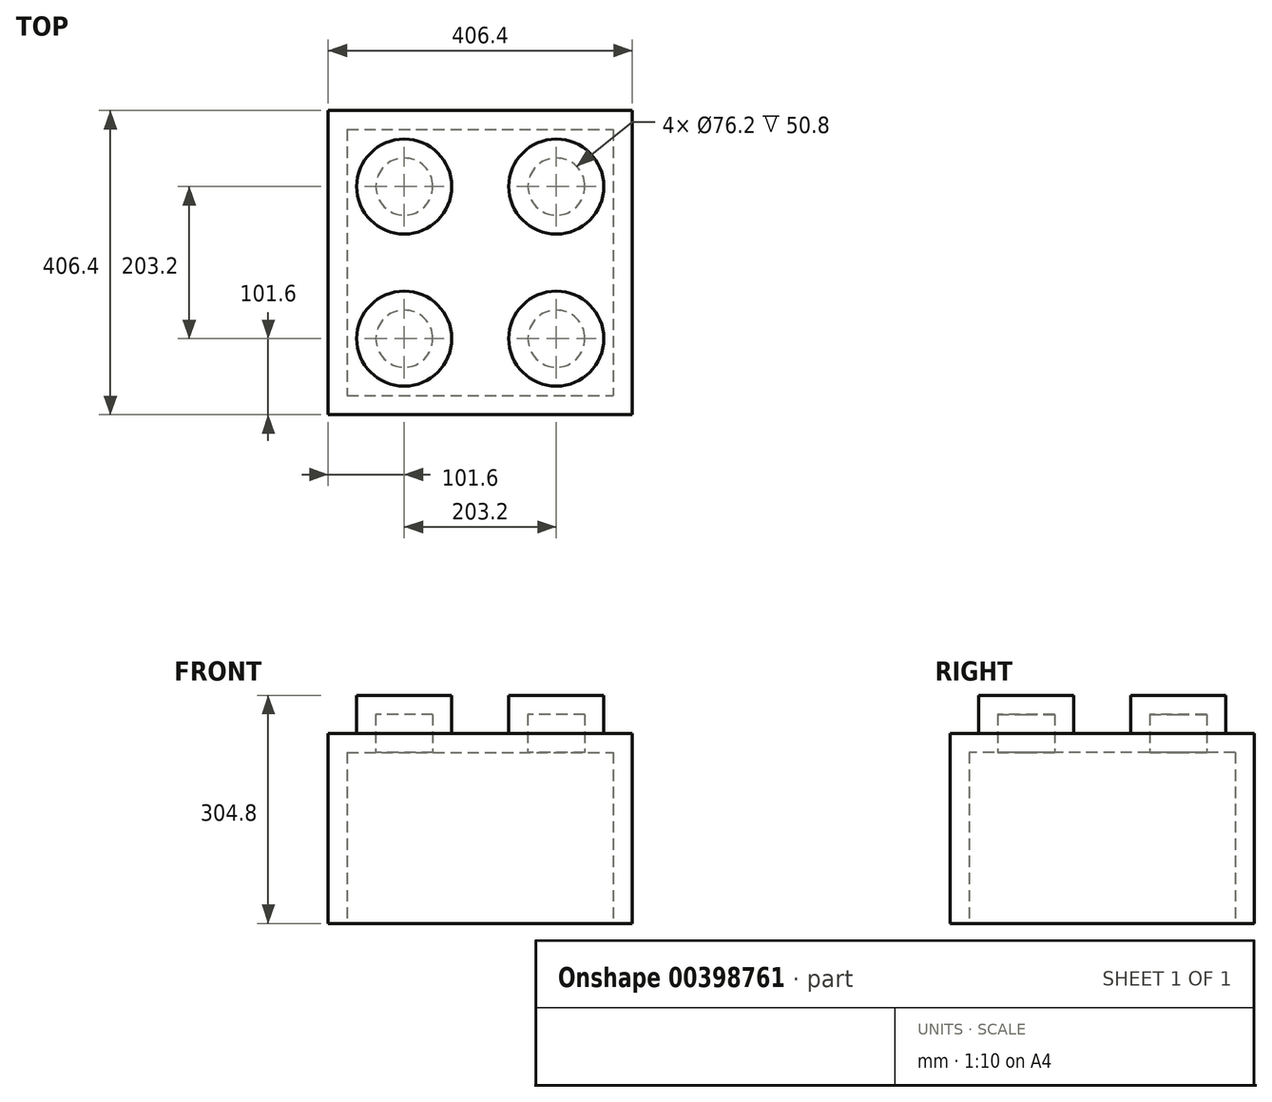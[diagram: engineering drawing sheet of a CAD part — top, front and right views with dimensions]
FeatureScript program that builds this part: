
annotation { "Feature Type Name" : "Feature", "Feature Type Description" : "" }
export const myFeature = defineFeature(function(context is Context, id is Id, definition is map)
    precondition{}
    {
        {
            var Q0;
            Q0=qCreatedBy(makeId("Top.planeOp"),FACE);
            var sketch = newSketch(context, id + "F0", { "sketchPlane" : qUnion([Q0])});
            skLineSegment(sketch, "E0.bottom", {"start": v(-203.2, 203.2) * mm, "end": v(203.2, 203.2) * mm});
            skLineSegment(sketch, "E0.top", {"start": v(-203.2, -203.2) * mm, "end": v(203.2, -203.2) * mm});
            skLineSegment(sketch, "E0.left", {"start": v(-203.2, 203.2) * mm, "end": v(-203.2, -203.2) * mm});
            skLineSegment(sketch, "E0.right", {"start": v(203.2, 203.2) * mm, "end": v(203.2, -203.2) * mm});
            skPoint(sketch, "E0.middle", {"position": v(0, 0) * mm});
            skSolve(sketch);
        }
        {
            var Q0;
            Q0 = qSketchRegion(id + "F0", true);
            extrude(context, id + "F1", {"entities" : qUnion([Q0]), "depth" : 254 * mm});
        }
        {
            var Q0;
            Q0=makeQuery(id+"F1.opExtrude","CAP_FACE",FACE,{"disambiguationData":[OSD([sQuery(id+"F0.wireOp",EDGE,"E0.bottom"),sQuery(id+"F0.wireOp",EDGE,"E0.top"),sQuery(id+"F0.wireOp",EDGE,"E0.left"),sQuery(id+"F0.wireOp",EDGE,"E0.right")])],"isStart":false});
            var sketch = newSketch(context, id + "F2", { "sketchPlane" : qUnion([Q0])});
            skLineSegment(sketch, "E1.0.0", {"start": v(-203.2, 203.2) * mm, "end": v(-203.2, -203.2) * mm, "construction": true});
            skLineSegment(sketch, "E1.0.1", {"start": v(-203.2, -203.2) * mm, "end": v(203.2, -203.2) * mm, "construction": true});
            skLineSegment(sketch, "E1.0.2", {"start": v(203.2, -203.2) * mm, "end": v(203.2, 203.2) * mm, "construction": true});
            skLineSegment(sketch, "E1.0.3", {"start": v(203.2, 203.2) * mm, "end": v(-203.2, 203.2) * mm, "construction": true});
            skCircle(sketch, "E2", {"center": v(101.6, 101.6) * mm, "radius": 63.5 * mm});
            skLineSegment(sketch, "E3", {"start": v(203.2, 203.2) * mm, "end": v(0, 0) * mm, "construction": true});
            skLineSegment(sketch, "E4", {"start": v(0, 0) * mm, "end": v(-203.2, -203.2) * mm, "construction": true});
            skLineSegment(sketch, "E5.1.0", {"start": v(0, 0) * mm, "end": v(203.2, -203.2) * mm, "construction": true});
            skLineSegment(sketch, "E5.1.1", {"start": v(-203.2, 203.2) * mm, "end": v(0, 0) * mm, "construction": true});
            skCircle(sketch, "E5.1.2", {"center": v(-101.6, 101.6) * mm, "radius": 63.5 * mm});
            skLineSegment(sketch, "E5.2.0", {"start": v(0, 0) * mm, "end": v(203.2, 203.2) * mm, "construction": true});
            skLineSegment(sketch, "E5.2.1", {"start": v(-203.2, -203.2) * mm, "end": v(0, 0) * mm, "construction": true});
            skCircle(sketch, "E5.2.2", {"center": v(-101.6, -101.6) * mm, "radius": 63.5 * mm});
            skLineSegment(sketch, "E5.3.0", {"start": v(0, 0) * mm, "end": v(-203.2, 203.2) * mm, "construction": true});
            skLineSegment(sketch, "E5.3.1", {"start": v(203.2, -203.2) * mm, "end": v(0, 0) * mm, "construction": true});
            skCircle(sketch, "E5.3.2", {"center": v(101.6, -101.6) * mm, "radius": 63.5 * mm});
            skPoint(sketch, "E5.center", {"position": v(0, 0) * mm});
            skSolve(sketch);
        }
        {
            var Q0;
            Q0=makeQuery(id+"F2.imprint","IMPRINT",FACE,{"disambiguationData":[TD([[makeQuery(id+"F2.imprint","IMPRINT",EDGE,{"derivedFrom":sQuery(id+"F2.wireOp",EDGE,"E2")}),1.0]])]});
            var Q1;
            Q1=makeQuery(id+"F2.imprint","IMPRINT",FACE,{"disambiguationData":[TD([[makeQuery(id+"F2.imprint","IMPRINT",EDGE,{"derivedFrom":sQuery(id+"F2.wireOp",EDGE,"E5.3.2")}),1.0]])]});
            var Q2;
            Q2=makeQuery(id+"F2.imprint","IMPRINT",FACE,{"disambiguationData":[TD([[makeQuery(id+"F2.imprint","IMPRINT",EDGE,{"derivedFrom":sQuery(id+"F2.wireOp",EDGE,"E5.2.2")}),1.0]])]});
            var Q3;
            Q3=makeQuery(id+"F2.imprint","IMPRINT",FACE,{"disambiguationData":[TD([[makeQuery(id+"F2.imprint","IMPRINT",EDGE,{"derivedFrom":sQuery(id+"F2.wireOp",EDGE,"E5.1.2")}),1.0]])]});
            extrude(context, id + "F3", {"entities" : qUnion([Q0, Q1, Q2, Q3]), "operationType" : NewBodyOperationType.ADD, "depth" : 50.8 * mm});
        }
        {
            var Q0;
            Q0=makeQuery(id+"F1.opExtrude","CAP_FACE",FACE,{"disambiguationData":[OSD([sQuery(id+"F0.wireOp",EDGE,"E0.bottom"),sQuery(id+"F0.wireOp",EDGE,"E0.top"),sQuery(id+"F0.wireOp",EDGE,"E0.left"),sQuery(id+"F0.wireOp",EDGE,"E0.right")])],"isStart":true});
            shell(context, id + "F4", {"entities" : qUnion([Q0]), "thickness" : 25.4 * mm});
        }
    });
